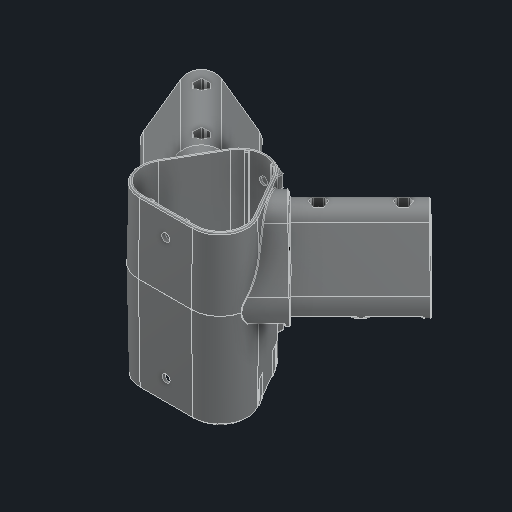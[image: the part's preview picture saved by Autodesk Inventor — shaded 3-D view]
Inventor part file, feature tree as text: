
AUTODESK INVENTOR PART (.ipt)
format: ipt  version: 2025 (Build 290162000, 162)  size: 2,533,888 bytes
history: native  units: in
note: dims shown in document units (in); Inventor stores cm internally (conversion verified against a paired STEP export)
features: fillet x1
ambient origin geometry x8: Origin, YZ Plane, XZ Plane, XY Plane, X Axis, Y Axis, Z Axis, Center Point
bodies: Solid1 (feature_tree)
feature tree (1):
  fillet  "Fillet138"  [1 undecoded]
note: 1 required parameter value undecoded (feature->parameter linkage not recoverable at this tier; creation-order binding heuristic only, values carry confidence <= 0.55)
